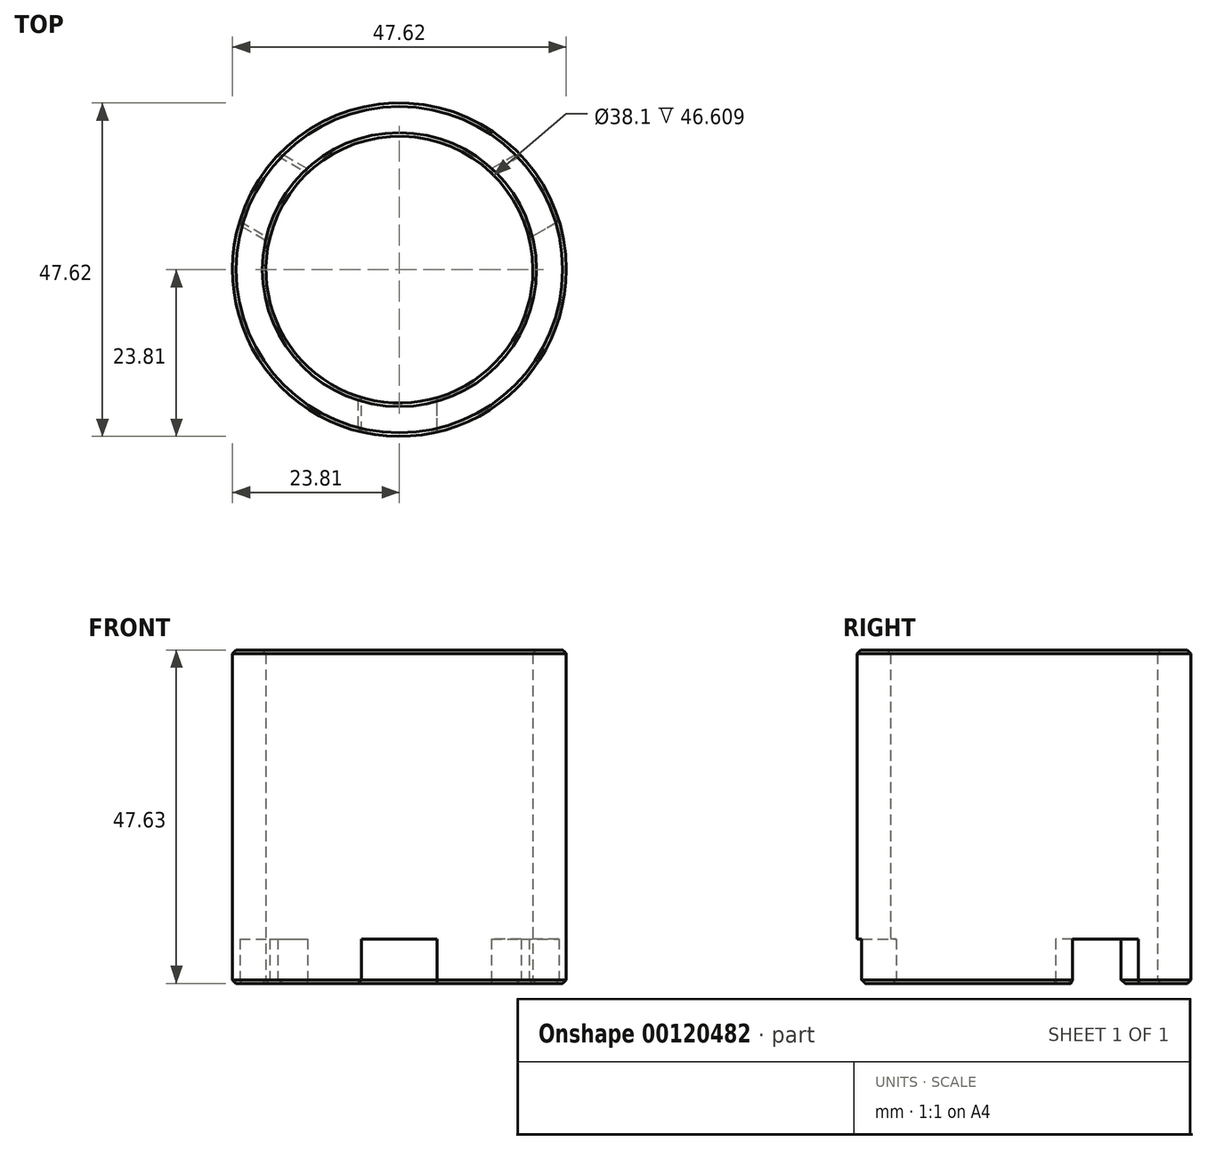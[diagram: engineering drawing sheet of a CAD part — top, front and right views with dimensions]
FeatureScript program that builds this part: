
annotation { "Feature Type Name" : "Feature", "Feature Type Description" : "" }
export const myFeature = defineFeature(function(context is Context, id is Id, definition is map)
    precondition{}
    {
        {
            var Q0;
            Q0=qCreatedBy(makeId("Top.planeOp"),FACE);
            var sketch = newSketch(context, id + "F0", { "sketchPlane" : qUnion([Q0])});
            skCircle(sketch, "E0", {"center": v(0, 0) * mm, "radius": 23.81 * mm});
            skCircle(sketch, "E1", {"center": v(0, 0) * mm, "radius": 19.05 * mm});
            skSolve(sketch);
        }
        {
            var Q0;
            Q0=makeQuery(id+"F0.imprint","IMPRINT",FACE,{"disambiguationData":[TD([[makeQuery(id+"F0.imprint","IMPRINT",EDGE,{"derivedFrom":sQuery(id+"F0.wireOp",EDGE,"E0")}),1.0]])]});
            extrude(context, id + "F1", {"entities" : qUnion([Q0]), "depth" : 47.62 * mm});
        }
        {
            var Q0;
            Q0=makeQuery(id+"F1.opExtrude","CAP_FACE",FACE,{"disambiguationData":[OSD([sQuery(id+"F0.wireOp",EDGE,"E0"),sQuery(id+"F0.wireOp",EDGE,"E1")])],"isStart":true});
            var sketch = newSketch(context, id + "F2", { "sketchPlane" : qUnion([Q0])});
            skLineSegment(sketch, "E2.bottom", {"start": v(-5.4, 23.81) * mm, "end": v(5.4, 23.81) * mm});
            skLineSegment(sketch, "E2.top", {"start": v(-5.4, 18.27) * mm, "end": v(5.4, 18.27) * mm});
            skLineSegment(sketch, "E2.left", {"start": v(-5.4, 23.81) * mm, "end": v(-5.4, 18.27) * mm});
            skLineSegment(sketch, "E2.right", {"start": v(5.4, 23.81) * mm, "end": v(5.4, 18.27) * mm});
            skLineSegment(sketch, "E3.1.0", {"start": v(-17.92, -16.58) * mm, "end": v(-23.32, -7.23) * mm});
            skLineSegment(sketch, "E3.1.1", {"start": v(-17.92, -16.58) * mm, "end": v(-13.12, -13.8) * mm});
            skLineSegment(sketch, "E3.1.2", {"start": v(-13.12, -13.8) * mm, "end": v(-18.52, -4.46) * mm});
            skLineSegment(sketch, "E3.1.3", {"start": v(-23.32, -7.23) * mm, "end": v(-18.52, -4.46) * mm});
            skLineSegment(sketch, "E3.2.0", {"start": v(23.32, -7.23) * mm, "end": v(17.92, -16.58) * mm});
            skLineSegment(sketch, "E3.2.1", {"start": v(23.32, -7.23) * mm, "end": v(18.52, -4.46) * mm});
            skLineSegment(sketch, "E3.2.2", {"start": v(18.52, -4.46) * mm, "end": v(13.12, -13.8) * mm});
            skLineSegment(sketch, "E3.2.3", {"start": v(17.92, -16.58) * mm, "end": v(13.12, -13.8) * mm});
            skPoint(sketch, "E3.center", {"position": v(0, 0) * mm});
            skSolve(sketch);
        }
        {
            var Q0;
            Q0 = qSketchRegion(id + "F2", true);
            extrude(context, id + "F3", {"entities" : qUnion([Q0]), "operationType" : NewBodyOperationType.REMOVE, "oppositeDirection" : true, "depth" : 6.35 * mm});
        }
        {
            var Q0;
            Q0=makeQuery(id+"F1.opExtrude","CAP_EDGE",EDGE,{"disambiguationData":[OSD([sQuery(id+"F0.wireOp",EDGE,"E0")])],"isStart":false});
            var Q1;
            Q1=makeQuery(id+"F1.opExtrude","CAP_EDGE",EDGE,{"disambiguationData":[OSD([sQuery(id+"F0.wireOp",EDGE,"E1")])],"isStart":false});
            var Q2;
            {var subQ0=sQuery(id+"F0.wireOp",EDGE,"E1");Q2=makeQuery(id+"F3.boolean.opBoolean","SPLIT",EDGE,{"disambiguationData":[TD([makeQuery(id+"F3.opExtrude","SWEPT_FACE",FACE,{"disambiguationData":[OSD([sQuery(id+"F2.wireOp",EDGE,"E2.left")])]})])],"derivedFrom":makeQuery(id+"F1.opExtrude","CAP_EDGE",EDGE,{"disambiguationData":[OSD([subQ0])],"isStart":true})});}
            var Q3;
            {var subQ0=sQuery(id+"F0.wireOp",EDGE,"E0");Q3=makeQuery(id+"F3.boolean.opBoolean","SPLIT",EDGE,{"disambiguationData":[TD([makeQuery(id+"F3.opExtrude","SWEPT_FACE",FACE,{"disambiguationData":[OSD([sQuery(id+"F2.wireOp",EDGE,"E2.left")])]})])],"derivedFrom":makeQuery(id+"F1.opExtrude","CAP_EDGE",EDGE,{"disambiguationData":[OSD([subQ0])],"isStart":true})});}
            var Q4;
            {var subQ0=sQuery(id+"F0.wireOp",EDGE,"E0");Q4=makeQuery(id+"F3.boolean.opBoolean","SPLIT",EDGE,{"disambiguationData":[TD([makeQuery(id+"F3.opExtrude","SWEPT_FACE",FACE,{"disambiguationData":[OSD([sQuery(id+"F2.wireOp",EDGE,"E2.right")])]})])],"derivedFrom":makeQuery(id+"F1.opExtrude","CAP_EDGE",EDGE,{"disambiguationData":[OSD([subQ0])],"isStart":true})});}
            var Q5;
            {var subQ0=sQuery(id+"F0.wireOp",EDGE,"E1");Q5=makeQuery(id+"F3.boolean.opBoolean","SPLIT",EDGE,{"disambiguationData":[TD([makeQuery(id+"F3.opExtrude","SWEPT_FACE",FACE,{"disambiguationData":[OSD([sQuery(id+"F2.wireOp",EDGE,"E2.right")])]})])],"derivedFrom":makeQuery(id+"F1.opExtrude","CAP_EDGE",EDGE,{"disambiguationData":[OSD([subQ0])],"isStart":true})});}
            var Q6;
            {var subQ0=sQuery(id+"F0.wireOp",EDGE,"E1");Q6=makeQuery(id+"F3.boolean.opBoolean","SPLIT",EDGE,{"disambiguationData":[TD([makeQuery(id+"F3.opExtrude","SWEPT_FACE",FACE,{"disambiguationData":[OSD([sQuery(id+"F2.wireOp",EDGE,"E3.1.1")])]})])],"derivedFrom":makeQuery(id+"F1.opExtrude","CAP_EDGE",EDGE,{"disambiguationData":[OSD([subQ0])],"isStart":true})});}
            var Q7;
            {var subQ0=sQuery(id+"F0.wireOp",EDGE,"E0");Q7=makeQuery(id+"F3.boolean.opBoolean","SPLIT",EDGE,{"disambiguationData":[TD([makeQuery(id+"F3.opExtrude","SWEPT_FACE",FACE,{"disambiguationData":[OSD([sQuery(id+"F2.wireOp",EDGE,"E3.1.1")])]})])],"derivedFrom":makeQuery(id+"F1.opExtrude","CAP_EDGE",EDGE,{"disambiguationData":[OSD([subQ0])],"isStart":true})});}
            var Q8;
            Q8=makeQuery(id+"F3.boolean.opBoolean","COPY",EDGE,{"derivedFrom":makeQuery(id+"F3.opExtrude","CAP_EDGE",EDGE,{"disambiguationData":[OSD([sQuery(id+"F2.wireOp",EDGE,"E3.1.3")])],"isStart":true})});
            var Q9;
            Q9=makeQuery(id+"F3.boolean.opBoolean","COPY",EDGE,{"derivedFrom":makeQuery(id+"F3.opExtrude","CAP_EDGE",EDGE,{"disambiguationData":[OSD([sQuery(id+"F2.wireOp",EDGE,"E2.left")])],"isStart":true})});
            var Q10;
            Q10=makeQuery(id+"F3.boolean.opBoolean","COPY",EDGE,{"derivedFrom":makeQuery(id+"F3.opExtrude","CAP_EDGE",EDGE,{"disambiguationData":[OSD([sQuery(id+"F2.wireOp",EDGE,"E2.right")])],"isStart":true})});
            var Q11;
            Q11=makeQuery(id+"F3.boolean.opBoolean","COPY",EDGE,{"derivedFrom":makeQuery(id+"F3.opExtrude","CAP_EDGE",EDGE,{"disambiguationData":[OSD([sQuery(id+"F2.wireOp",EDGE,"E3.2.1")])],"isStart":true})});
            var Q12;
            Q12=makeQuery(id+"F3.boolean.opBoolean","COPY",EDGE,{"derivedFrom":makeQuery(id+"F3.opExtrude","CAP_EDGE",EDGE,{"disambiguationData":[OSD([sQuery(id+"F2.wireOp",EDGE,"E3.2.3")])],"isStart":true})});
            var Q13;
            Q13=makeQuery(id+"F3.boolean.opBoolean","COPY",EDGE,{"derivedFrom":makeQuery(id+"F3.opExtrude","CAP_EDGE",EDGE,{"disambiguationData":[OSD([sQuery(id+"F2.wireOp",EDGE,"E3.1.1")])],"isStart":true})});
            chamfer(context, id + "F4", {"entities" : qUnion([Q0, Q1, Q2, Q3, Q4, Q5, Q6, Q7, Q8, Q9, Q10, Q11, Q12, Q13]), "width" : 0.5 * mm, "tangentPropagation" : true});
        }
    });
